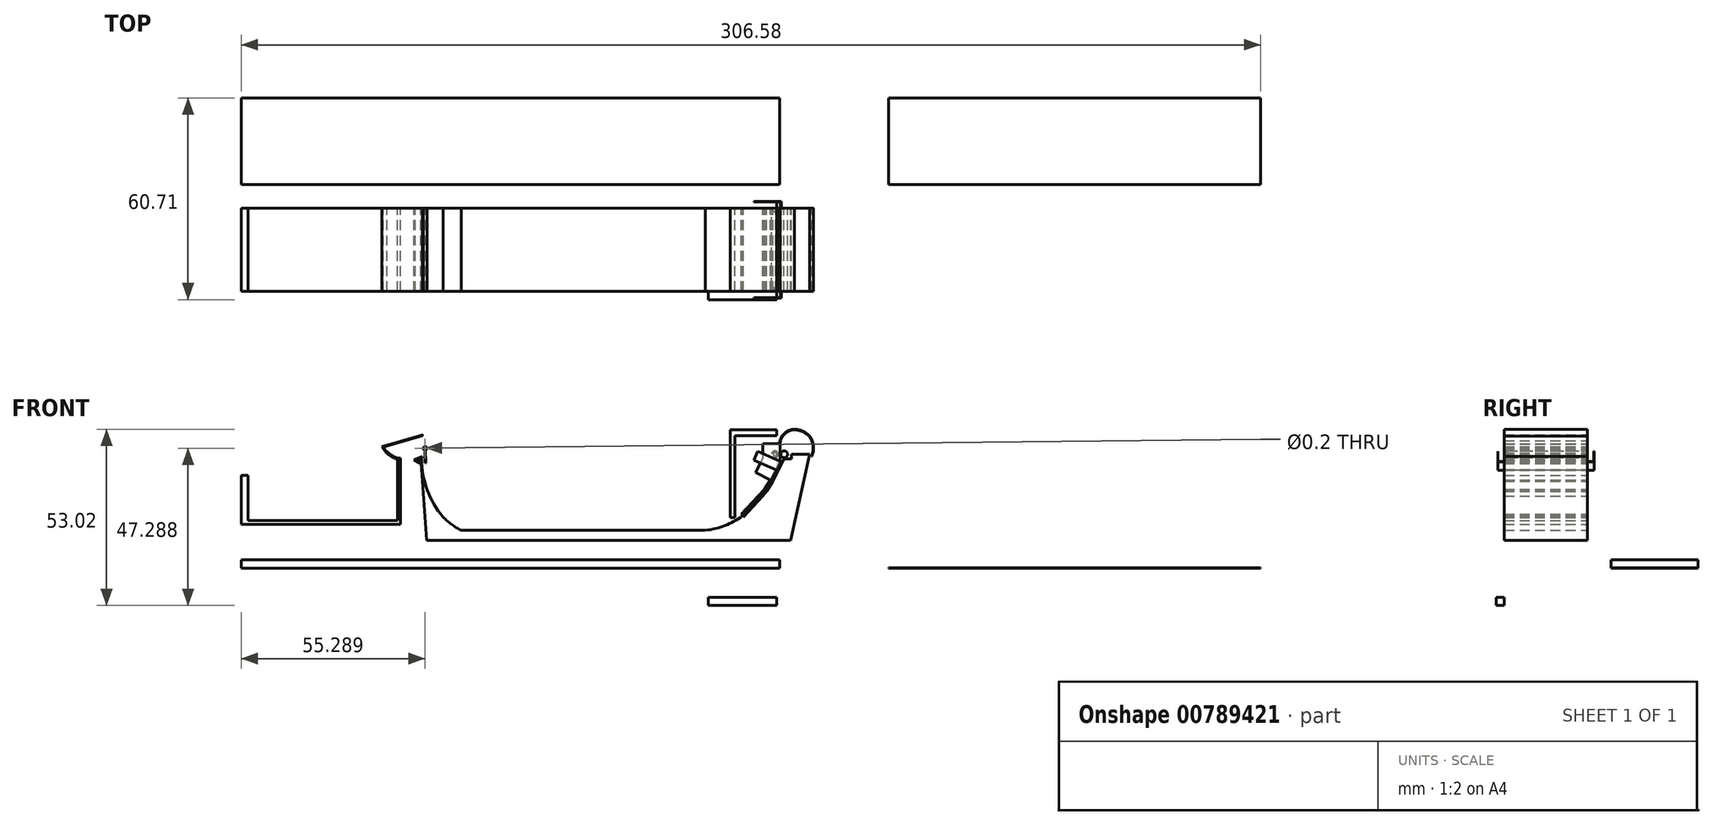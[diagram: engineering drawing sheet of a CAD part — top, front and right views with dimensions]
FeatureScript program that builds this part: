
annotation { "Feature Type Name" : "Feature", "Feature Type Description" : "" }
export const myFeature = defineFeature(function(context is Context, id is Id, definition is map)
    precondition{}
    {
        {
            var Q0;
            Q0=qCreatedBy(makeId("Front.planeOp"),FACE);
            var sketch = newSketch(context, id + "F0", { "sketchPlane" : qUnion([Q0])});
            skLineSegment(sketch, "E0", {"start": v(-36.24, 27.85) * mm, "end": v(-38.27, 27.85) * mm});
            skLineSegment(sketch, "E1", {"start": v(-38.27, 27.85) * mm, "end": v(-38.27, 17.8) * mm});
            skPoint(sketch, "E2.startSnap0", {"position": v(14.17, 40.62) * mm});
            skPoint(sketch, "E3.second.point", {"position": v(15.63, 39.33) * mm});
            skPoint(sketch, "E3.third.point", {"position": v(16.42, 39.16) * mm});
            skPoint(sketch, "E4.end.orphan", {"position": v(0, 14.33) * mm});
            skLineSegment(sketch, "E5", {"start": v(-36.24, 27.85) * mm, "end": v(-36.24, 19.36) * mm});
            skPoint(sketch, "E6.orphan", {"position": v(-34.21, 27.85) * mm});
            skPoint(sketch, "E7.centerSnap0", {"position": v(17.02, 36.74) * mm});
            skPoint(sketch, "E8.orphan", {"position": v(17.66, 36.74) * mm});
            skPoint(sketch, "E9.orphan", {"position": v(16.38, 36.74) * mm});
            skPoint(sketch, "E10.orphan", {"position": v(17.66, 36.62) * mm});
            skPoint(sketch, "E11.start.orphan", {"position": v(16.38, 36.62) * mm});
            skLineSegment(sketch, "E12", {"start": v(15.74, 32.9) * mm, "end": v(15.83, 31.65) * mm});
            skLineSegment(sketch, "E13", {"start": v(17.46, 8.3) * mm, "end": v(83.3, 8.3) * mm});
            skLineSegment(sketch, "E14", {"start": v(83.3, 8.3) * mm, "end": v(127.03, 8.3) * mm});
            skLineSegment(sketch, "E15", {"start": v(127.03, 8.3) * mm, "end": v(132.63, 34.27) * mm});
            skLineSegment(sketch, "E16", {"start": v(101.32, 11.34) * mm, "end": v(27.93, 11.34) * mm});
            skArc(sketch, "E17", {"start": v(15.97, 32.9) * mm, "mid": v(17.65, 23.56) * mm, "end": v(22.41, 15.34) * mm});
            skLineSegment(sketch, "E18", {"start": v(15.97, 32.9) * mm, "end": v(15.74, 32.9) * mm});
            skPoint(sketch, "E19.orphan", {"position": v(17.66, 36.03) * mm});
            skPoint(sketch, "E20.orphan", {"position": v(16.38, 36.03) * mm});
            skPoint(sketch, "E21.start.orphan", {"position": v(15.63, 40.62) * mm});
            skLineSegment(sketch, "E22", {"start": v(16.94, 35.48) * mm, "end": v(16.96, 35.48) * mm});
            skPoint(sketch, "E23.start.orphan", {"position": v(16.96, 31.74) * mm});
            skArc(sketch, "E24", {"start": v(16.18, 39.88) * mm, "mid": v(16.3, 39.98) * mm, "end": v(16.18, 40.08) * mm});
            skCircle(sketch, "E25", {"center": v(17.02, 36.03) * mm, "radius": 0.1 * mm});
            skLineSegment(sketch, "E26", {"start": v(17.16, 31.54) * mm, "end": v(17.09, 31.54) * mm});
            skLineSegment(sketch, "E27", {"start": v(17.09, 31.54) * mm, "end": v(17.04, 35.85) * mm});
            skLineSegment(sketch, "E28", {"start": v(17.04, 35.85) * mm, "end": v(17, 35.84) * mm});
            skLineSegment(sketch, "E29", {"start": v(17, 35.84) * mm, "end": v(17.04, 31.54) * mm});
            skLineSegment(sketch, "E30", {"start": v(17.04, 31.54) * mm, "end": v(16.96, 31.54) * mm});
            skLineSegment(sketch, "E31", {"start": v(16.96, 31.54) * mm, "end": v(16.94, 35.49) * mm});
            skLineSegment(sketch, "E32", {"start": v(13.75, 43.8) * mm, "end": v(16.18, 40.08) * mm});
            skPoint(sketch, "E33.start.orphan", {"position": v(1.3, 38.23) * mm});
            skPoint(sketch, "E34.end.orphan", {"position": v(2.06, 38.23) * mm});
            skPoint(sketch, "E35.orphan", {"position": v(15.34, 39.98) * mm});
            skPoint(sketch, "E36.start.orphan", {"position": v(17.02, 36.62) * mm});
            skPoint(sketch, "E37.trimOffspring.end.orphan", {"position": v(17.58, 36.03) * mm});
            skArc(sketch, "E38", {"start": v(17.14, 35.5) * mm, "mid": v(17, 36.57) * mm, "end": v(16.94, 35.49) * mm});
            skLineSegment(sketch, "E39", {"start": v(17.14, 35.5) * mm, "end": v(17.21, 31.54) * mm});
            skLineSegment(sketch, "E40", {"start": v(17.21, 31.54) * mm, "end": v(17.16, 31.54) * mm});
            skPoint(sketch, "E41.orphan", {"position": v(2.06, 39.98) * mm});
            skArc(sketch, "E42", {"start": v(22.41, 15.34) * mm, "mid": v(25, 13.1) * mm, "end": v(27.93, 11.34) * mm});
            skLineSegment(sketch, "E43", {"start": v(106.36, 11.34) * mm, "end": v(106.36, 11.34) * mm});
            skPoint(sketch, "E44.end.orphan", {"position": v(2.65, 14.33) * mm});
            skPoint(sketch, "E44.start.orphan", {"position": v(2.65, 11.02) * mm});
            skPoint(sketch, "E45.end.orphan", {"position": v(0, 8.98) * mm});
            skPoint(sketch, "E45.start.orphan", {"position": v(4.08, 8.98) * mm});
            skPoint(sketch, "E46.end.orphan", {"position": v(-16.48, 8.98) * mm});
            skPoint(sketch, "E47.start.orphan", {"position": v(-36.24, 10.87) * mm});
            skPoint(sketch, "E48.end.orphan", {"position": v(-38.27, 8.98) * mm});
            skPoint(sketch, "E48.start.orphan", {"position": v(-38.27, 14.33) * mm});
            skLineSegment(sketch, "E49", {"start": v(4.08, 13.15) * mm, "end": v(-38.27, 13.15) * mm});
            skLineSegment(sketch, "E50", {"start": v(-38.27, 13.15) * mm, "end": v(-38.27, 17.8) * mm});
            skLineSegment(sketch, "E51", {"start": v(-36.24, 17.8) * mm, "end": v(-36.24, 14.33) * mm});
            skLineSegment(sketch, "E52", {"start": v(-36.24, 13.15) * mm, "end": v(2.65, 13.15) * mm});
            skLineSegment(sketch, "E53", {"start": v(-36.24, 14.33) * mm, "end": v(2.65, 14.33) * mm});
            skLineSegment(sketch, "E54", {"start": v(-36.24, 17.8) * mm, "end": v(-36.24, 19.36) * mm});
            skPoint(sketch, "E55.orphan", {"position": v(11.11, 39.83) * mm});
            skPoint(sketch, "E56.orphan", {"position": v(2.68, 38.35) * mm});
            skPoint(sketch, "E57.orphan", {"position": v(2.86, 38.35) * mm});
            skLineSegment(sketch, "E58", {"start": v(3.18, 14.33) * mm, "end": v(2.65, 14.33) * mm});
            skLineSegment(sketch, "E59", {"start": v(4.08, 13.15) * mm, "end": v(5.21, 13.15) * mm});
            skLineSegment(sketch, "E60", {"start": v(3.18, 14.33) * mm, "end": v(4.08, 14.33) * mm});
            skPoint(sketch, "E61.start.orphan", {"position": v(4.08, 34.96) * mm});
            skPoint(sketch, "E62.orphan", {"position": v(4.08, 34.48) * mm});
            skLineSegment(sketch, "E63", {"start": v(16.18, 39.88) * mm, "end": v(6.67, 37.05) * mm});
            skLineSegment(sketch, "E64", {"start": v(16.18, 40.08) * mm, "end": v(15.51, 39.87) * mm});
            skLineSegment(sketch, "E65", {"start": v(15.51, 39.87) * mm, "end": v(6.6, 37.22) * mm});
            skLineSegment(sketch, "E66", {"start": v(6.6, 37.22) * mm, "end": v(4.09, 36.47) * mm});
            skPoint(sketch, "E66.endSnap0", {"position": v(3.22, 38.25) * mm});
            skLineSegment(sketch, "E67", {"start": v(6.67, 37.05) * mm, "end": v(4.41, 36.38) * mm});
            skArc(sketch, "E68", {"start": v(5.56, 34.55) * mm, "mid": v(5.56, 34.55) * mm, "end": v(5.57, 34.55) * mm});
            skLineSegment(sketch, "E69", {"start": v(5.57, 34.55) * mm, "end": v(5.57, 34.54) * mm});
            skPoint(sketch, "E70.orphan", {"position": v(13.65, 39.85) * mm});
            skPoint(sketch, "E71.start.orphan", {"position": v(3.22, 36.22) * mm});
            skLineSegment(sketch, "E72", {"start": v(4.08, 14.33) * mm, "end": v(8.74, 14.33) * mm});
            skLineSegment(sketch, "E73", {"start": v(8.74, 14.33) * mm, "end": v(8.74, 32.67) * mm});
            skLineSegment(sketch, "E74", {"start": v(8.74, 33.1) * mm, "end": v(9.64, 33.1) * mm});
            skLineSegment(sketch, "E75", {"start": v(9.64, 33.1) * mm, "end": v(9.64, 13.15) * mm});
            skLineSegment(sketch, "E76", {"start": v(9.64, 13.15) * mm, "end": v(5.21, 13.15) * mm});
            skArc(sketch, "E77", {"start": v(4.41, 36.38) * mm, "mid": v(6.3, 34.38) * mm, "end": v(8.74, 33.1) * mm});
            skArc(sketch, "E78", {"start": v(4.09, 36.47) * mm, "mid": v(6.04, 34.12) * mm, "end": v(8.74, 32.67) * mm});
            skArc(sketch, "E79", {"start": v(101.32, 11.34) * mm, "mid": v(107.16, 12.76) * mm, "end": v(112.43, 15.65) * mm});
            skCircle(sketch, "E80", {"center": v(122.26, 34.23) * mm, "radius": 1 * mm});
            skLineSegment(sketch, "E81", {"start": v(110.26, 39.86) * mm, "end": v(110.26, 15.22) * mm});
            skLineSegment(sketch, "E82", {"start": v(110.26, 15.22) * mm, "end": v(108.83, 15.22) * mm});
            skLineSegment(sketch, "E83", {"start": v(108.83, 15.22) * mm, "end": v(108.83, 39.86) * mm});
            skLineSegment(sketch, "E84", {"start": v(108.83, 39.86) * mm, "end": v(108.83, 41.61) * mm});
            skLineSegment(sketch, "E85", {"start": v(108.83, 41.61) * mm, "end": v(122.82, 41.61) * mm});
            skCircle(sketch, "E86", {"center": v(125.03, 34.23) * mm, "radius": 1.03 * mm});
            skLineSegment(sketch, "E87", {"start": v(127.23, 34.27) * mm, "end": v(127.23, 32.8) * mm});
            skLineSegment(sketch, "E88", {"start": v(127.23, 32.8) * mm, "end": v(124.93, 32.8) * mm});
            skLineSegment(sketch, "E89", {"start": v(123.58, 37.49) * mm, "end": v(123.58, 32.21) * mm});
            skLineSegment(sketch, "E90", {"start": v(123.74, 32.21) * mm, "end": v(123.74, 37.22) * mm});
            skLineSegment(sketch, "E91", {"start": v(122.82, 41.61) * mm, "end": v(122.82, 39.86) * mm});
            skLineSegment(sketch, "E92.trimOffspring", {"start": v(122.82, 39.86) * mm, "end": v(110.26, 39.86) * mm});
            skArc(sketch, "E93", {"start": v(128.06, 41.59) * mm, "mid": v(125.07, 40.23) * mm, "end": v(123.74, 37.22) * mm});
            skArc(sketch, "E94", {"start": v(132.54, 39.67) * mm, "mid": v(130.48, 41.05) * mm, "end": v(128.06, 41.59) * mm});
            skArc(sketch, "E95", {"start": v(133.2, 33.63) * mm, "mid": v(133.7, 36.74) * mm, "end": v(132.54, 39.67) * mm});
            skArc(sketch, "E96", {"start": v(133.37, 33.63) * mm, "mid": v(133.79, 36.77) * mm, "end": v(132.69, 39.74) * mm});
            skArc(sketch, "E97", {"start": v(132.69, 39.74) * mm, "mid": v(130.57, 41.2) * mm, "end": v(128.06, 41.76) * mm});
            skArc(sketch, "E98", {"start": v(128.06, 41.76) * mm, "mid": v(125.33, 40.75) * mm, "end": v(123.74, 38.31) * mm});
            skLineSegment(sketch, "E99", {"start": v(133.2, 33.63) * mm, "end": v(133.37, 33.63) * mm});
            skFitSpline(sketch, "E100", {"points": [v(123.74, 38.31) * mm, v(123.58, 37.45) * mm, v(123.58, 37.49) * mm, v(123.58, 37.86) * mm], "startDerivative": vector(-0.4, -2.37) * mm, "endDerivative": vector(0, 1.27) * mm});
            skPoint(sketch, "E101.end.orphan", {"position": v(123.58, 39.58) * mm});
            skPoint(sketch, "E101.start.orphan", {"position": v(123.74, 39.58) * mm});
            skLineSegment(sketch, "E102", {"start": v(127.23, 34.27) * mm, "end": v(132.63, 34.27) * mm});
            skPoint(sketch, "E103.end.orphan", {"position": v(127.23, 36.3) * mm});
            skLineSegment(sketch, "E104", {"start": v(123.58, 32.21) * mm, "end": v(122.49, 29.63) * mm});
            skLineSegment(sketch, "E105", {"start": v(123.74, 32.21) * mm, "end": v(122.62, 29.57) * mm});
            skLineSegment(sketch, "E106", {"start": v(122.62, 29.57) * mm, "end": v(121.09, 26.45) * mm});
            skLineSegment(sketch, "E107", {"start": v(120.93, 26.52) * mm, "end": v(122.49, 29.63) * mm});
            skLineSegment(sketch, "E108", {"start": v(121.09, 26.45) * mm, "end": v(119.27, 23.56) * mm});
            skLineSegment(sketch, "E109", {"start": v(119.07, 23.69) * mm, "end": v(120.93, 26.52) * mm});
            skLineSegment(sketch, "E110", {"start": v(119.27, 23.56) * mm, "end": v(112.33, 15.9) * mm});
            skLineSegment(sketch, "E111", {"start": v(112.33, 15.9) * mm, "end": v(112.07, 16.14) * mm});
            skLineSegment(sketch, "E112", {"start": v(112.07, 16.14) * mm, "end": v(119.07, 23.69) * mm});
            skLineSegment(sketch, "E113", {"start": v(112.58, 15.51) * mm, "end": v(112.43, 15.65) * mm});
            skLineSegment(sketch, "E114", {"start": v(124.93, 32.8) * mm, "end": v(121.63, 26.17) * mm});
            skLineSegment(sketch, "E115", {"start": v(121.63, 26.17) * mm, "end": v(119.75, 23.08) * mm});
            skLineSegment(sketch, "E116", {"start": v(119.75, 23.08) * mm, "end": v(118.52, 21.7) * mm});
            skLineSegment(sketch, "E117", {"start": v(118.52, 21.7) * mm, "end": v(114.05, 16.77) * mm});
            skLineSegment(sketch, "E118", {"start": v(114.05, 16.77) * mm, "end": v(112.74, 15.32) * mm});
            skLineSegment(sketch, "E119", {"start": v(112.74, 15.32) * mm, "end": v(112.58, 15.51) * mm});
            skLineSegment(sketch, "E120", {"start": v(123.94, 32.07) * mm, "end": v(122.8, 29.48) * mm});
            skLineSegment(sketch, "E121", {"start": v(122.8, 29.48) * mm, "end": v(122.96, 29.4) * mm});
            skLineSegment(sketch, "E122", {"start": v(122.96, 29.4) * mm, "end": v(124.2, 31.92) * mm});
            skLineSegment(sketch, "E123", {"start": v(124.2, 31.92) * mm, "end": v(123.94, 32.07) * mm});
            skArc(sketch, "E124", {"start": v(14.12, 32.5) * mm, "mid": v(14.94, 32) * mm, "end": v(15.83, 31.65) * mm});
            skArc(sketch, "E125", {"start": v(13.68, 32.53) * mm, "mid": v(14.7, 31.87) * mm, "end": v(15.84, 31.4) * mm});
            skLineSegment(sketch, "E126.trimOffspring", {"start": v(15.84, 31.4) * mm, "end": v(17.46, 8.3) * mm});
            skLineSegment(sketch, "E127", {"start": v(14.12, 32.5) * mm, "end": v(16.04, 33.27) * mm});
            skPoint(sketch, "E127.startSnap0", {"position": v(14.28, 32.4) * mm});
            skArc(sketch, "E128", {"start": v(16.03, 33.27) * mm, "mid": v(16.09, 33.4) * mm, "end": v(15.95, 33.45) * mm});
            skPoint(sketch, "E129.orphan", {"position": v(13.86, 32.4) * mm});
            skLineSegment(sketch, "E130", {"start": v(15.97, 33.46) * mm, "end": v(13.68, 32.53) * mm});
            skSolve(sketch);
        }
        {
            var Q0;
            Q0=makeQuery(id+"F0.imprint","IMPRINT",FACE,{"disambiguationData":[TD([[makeQuery(id+"F0.imprint","IMPRINT",EDGE,{"derivedFrom":sQuery(id+"F0.wireOp",EDGE,"E24")}),1.0]])]});
            extrude(context, id + "F1", {"entities" : qUnion([Q0]), "depth" : 25 * mm, "offsetDistance" : 25 * mm});
        }
        {
            var Q0;
            Q0=makeQuery(id+"F0.imprint","IMPRINT",FACE,{"disambiguationData":[TD([[makeQuery(id+"F0.imprint","IMPRINT",EDGE,{"derivedFrom":sQuery(id+"F0.wireOp",EDGE,"E25")}),-1.0]])]});
            extrude(context, id + "F2", {"entities" : qUnion([Q0]), "depth" : 25 * mm, "offsetDistance" : 25 * mm});
        }
        {
            var Q0;
            Q0=makeQuery(id+"F0.imprint","IMPRINT",FACE,{"disambiguationData":[TD([[makeQuery(id+"F0.imprint","IMPRINT",EDGE,{"derivedFrom":sQuery(id+"F0.wireOp",EDGE,"E12")}),1.0]])]});
            extrude(context, id + "F3", {"entities" : qUnion([Q0]), "depth" : 25 * mm, "offsetDistance" : 25 * mm});
        }
        {
            var Q0;
            Q0=qCreatedBy(makeId("Top.planeOp"),FACE);
            var sketch = newSketch(context, id + "F4", { "sketchPlane" : qUnion([Q0])});
            skLineSegment(sketch, "E131.bottom", {"start": v(-38.21, 33.2) * mm, "end": v(79.97, 33.2) * mm});
            skLineSegment(sketch, "E131.top", {"start": v(-38.21, 7.08) * mm, "end": v(79.97, 7.08) * mm});
            skLineSegment(sketch, "E131.left", {"start": v(-38.21, 33.2) * mm, "end": v(-38.21, 7.08) * mm});
            skLineSegment(sketch, "E132", {"start": v(62.88, 33.2) * mm, "end": v(123.68, 33.2) * mm});
            skLineSegment(sketch, "E133", {"start": v(123.68, 33.2) * mm, "end": v(123.68, 7.08) * mm});
            skLineSegment(sketch, "E134", {"start": v(123.68, 7.08) * mm, "end": v(79.97, 7.08) * mm});
            skLineSegment(sketch, "E135.bottom", {"start": v(156.42, 33.2) * mm, "end": v(268.31, 33.2) * mm});
            skLineSegment(sketch, "E135.top", {"start": v(156.42, 7.08) * mm, "end": v(268.31, 7.08) * mm});
            skLineSegment(sketch, "E135.left", {"start": v(156.42, 33.2) * mm, "end": v(156.42, 7.08) * mm});
            skLineSegment(sketch, "E135.right", {"start": v(268.31, 33.2) * mm, "end": v(268.31, 7.08) * mm});
            skSolve(sketch);
        }
        {
            var Q0;
            Q0=makeQuery(id+"F4.imprint","IMPRINT",FACE,{"disambiguationData":[TD([[makeQuery(id+"F4.imprint","IMPRINT",EDGE,{"derivedFrom":sQuery(id+"F4.wireOp",EDGE,"E131.bottom")}),-1.0]])]});
            extrude(context, id + "F5", {"entities" : qUnion([Q0]), "depth" : 2.5 * mm, "offsetDistance" : 25 * mm});
        }
        {
            var Q0;
            Q0=makeQuery(id+"F5.opExtrude","CAP_FACE",FACE,{"disambiguationData":[OSD([sQuery(id+"F4.wireOp",EDGE,"E131.bottom"),sQuery(id+"F4.wireOp",EDGE,"E131.top"),sQuery(id+"F4.wireOp",EDGE,"E131.left"),sQuery(id+"F4.wireOp",EDGE,"E132"),sQuery(id+"F4.wireOp",EDGE,"E133"),sQuery(id+"F4.wireOp",EDGE,"E134")])],"isStart":false});
            var sketch = newSketch(context, id + "F6", { "sketchPlane" : qUnion([Q0])});
            skLineSegment(sketch, "E136.bottom", {"start": v(-38.21, 33.2) * mm, "end": v(2.43, 33.2) * mm});
            skLineSegment(sketch, "E136.top", {"start": v(-38.21, 7.08) * mm, "end": v(2.43, 7.08) * mm});
            skLineSegment(sketch, "E136.left", {"start": v(-38.21, 33.2) * mm, "end": v(-38.21, 7.08) * mm});
            skLineSegment(sketch, "E136.right", {"start": v(2.43, 33.2) * mm, "end": v(2.43, 7.08) * mm});
            skSolve(sketch);
        }
        {
            var Q0;
            Q0=makeQuery(id+"F4.imprint","IMPRINT",FACE,{"disambiguationData":[TD([[makeQuery(id+"F4.imprint","IMPRINT",EDGE,{"derivedFrom":sQuery(id+"F4.wireOp",EDGE,"E135.bottom")}),-1.0]])]});
            extrude(context, id + "F7", {"entities" : qUnion([Q0]), "depth" : 0.1 * mm, "offsetDistance" : 25 * mm});
        }
        {
            var Q0;
            Q0=makeQuery(id+"F7.opExtrude","CAP_FACE",FACE,{"disambiguationData":[OSD([sQuery(id+"F4.wireOp",EDGE,"E135.bottom"),sQuery(id+"F4.wireOp",EDGE,"E135.top"),sQuery(id+"F4.wireOp",EDGE,"E135.left"),sQuery(id+"F4.wireOp",EDGE,"E135.right")])],"isStart":false});
            var sketch = newSketch(context, id + "F8", { "sketchPlane" : qUnion([Q0])});
            skLineSegment(sketch, "E137", {"start": v(161.42, 33.2) * mm, "end": v(161.42, 7.08) * mm});
            skSolve(sketch);
        }
        {
            var Q0;
            Q0=makeQuery(id+"F0.imprint","IMPRINT",FACE,{"disambiguationData":[TD([[makeQuery(id+"F0.imprint","IMPRINT",EDGE,{"derivedFrom":sQuery(id+"F0.wireOp",EDGE,"E80")}),1.0]])]});
            extrude(context, id + "F9", {"entities" : qUnion([Q0]), "depth" : 24 * mm, "offsetDistance" : 25 * mm});
        }
        {
            var Q0;
            Q0=makeQuery(id+"F0.imprint","IMPRINT",FACE,{"disambiguationData":[TD([[makeQuery(id+"F0.imprint","IMPRINT",EDGE,{"derivedFrom":sQuery(id+"F0.wireOp",EDGE,"E86")}),1.0]])]});
            extrude(context, id + "F10", {"entities" : qUnion([Q0]), "depth" : 25 * mm, "offsetDistance" : 25 * mm});
        }
        {
            var Q0;
            Q0=makeQuery(id+"F0.imprint","IMPRINT",FACE,{"disambiguationData":[TD([[makeQuery(id+"F0.imprint","IMPRINT",EDGE,{"derivedFrom":sQuery(id+"F0.wireOp",EDGE,"E89")}),1.0]])]});
            extrude(context, id + "F11", {"entities" : qUnion([Q0]), "depth" : 25 * mm, "offsetDistance" : 25 * mm});
        }
        {
            var Q0;
            Q0=makeQuery(id+"F3.opExtrude","CAP_FACE",FACE,{"disambiguationData":[OSD([sQuery(id+"F0.wireOp",EDGE,"E12"),sQuery(id+"F0.wireOp",EDGE,"E13"),sQuery(id+"F0.wireOp",EDGE,"E14"),sQuery(id+"F0.wireOp",EDGE,"E15"),sQuery(id+"F0.wireOp",EDGE,"w4MDjuLF-quGd-ABje-a59T-MTtNCKjQTqCC"),sQuery(id+"F0.wireOp",EDGE,"1qvucnDc-VQm0-8KhS-z7SF-FsArdJ4ZOjVe"),sQuery(id+"F0.wireOp",EDGE,"E16"),sQuery(id+"F0.wireOp",EDGE,"E17"),sQuery(id+"F0.wireOp",EDGE,"E18"),sQuery(id+"F0.wireOp",EDGE,"E42"),sQuery(id+"F0.wireOp",EDGE,"E79"),sQuery(id+"F0.wireOp",EDGE,"gqOQFJSQ-Navi-1Wbq-EMwf-l3DRoNK6dP6c"),sQuery(id+"F0.wireOp",EDGE,"E81"),sQuery(id+"F0.wireOp",EDGE,"E82"),sQuery(id+"F0.wireOp",EDGE,"E83"),sQuery(id+"F0.wireOp",EDGE,"E84"),sQuery(id+"F0.wireOp",EDGE,"E85"),sQuery(id+"F0.wireOp",EDGE,"473c3927-8e2a-4cfb-948c-3dfecc8dc65e.trimOffspring"),sQuery(id+"F0.wireOp",EDGE,"E103"),sQuery(id+"F0.wireOp",EDGE,"E87"),sQuery(id+"F0.wireOp",EDGE,"E88"),sQuery(id+"F0.wireOp",EDGE,"4562d8f3-b021-441a-b61c-79b72f4f745d.trimOffspring")])],"isStart":false});
            var sketch = newSketch(context, id + "F12", { "sketchPlane" : qUnion([Q0])});
            skLineSegment(sketch, "E138", {"start": v(127.03, 8.3) * mm, "end": v(122.8, -11.26) * mm});
            skLineSegment(sketch, "E139", {"start": v(122.8, -11.26) * mm, "end": v(120.3, -11.26) * mm});
            skLineSegment(sketch, "E140", {"start": v(122.8, -11.26) * mm, "end": v(122.8, -8.76) * mm});
            skLineSegment(sketch, "E141", {"start": v(122.8, -8.76) * mm, "end": v(120.3, -8.76) * mm});
            skLineSegment(sketch, "E142", {"start": v(120.3, -8.76) * mm, "end": v(120.3, -11.26) * mm});
            skLineSegment(sketch, "E143", {"start": v(120.3, -11.26) * mm, "end": v(122.8, -11.26) * mm});
            skSolve(sketch);
        }
        {
            var Q0;
            Q0=makeQuery(id+"F12.imprint","IMPRINT",FACE,{"disambiguationData":[TD([[makeQuery(id+"F12.imprint","IMPRINT",EDGE,{"derivedFrom":sQuery(id+"F12.wireOp",EDGE,"E140")}),1.0]])]});
            extrude(context, id + "F13", {"entities" : qUnion([Q0]), "operationType" : NewBodyOperationType.ADD, "depth" : 2.5 * mm, "offsetDistance" : 25 * mm});
        }
        {
            var Q0;
            Q0=makeQuery(id+"F13.opExtrude","SWEPT_FACE",FACE,{"disambiguationData":[OSD([sQuery(id+"F12.wireOp",EDGE,"E142")])]});
            extrude(context, id + "F14", {"entities" : qUnion([Q0]), "operationType" : NewBodyOperationType.ADD, "depth" : 18.1 * mm, "offsetDistance" : 25 * mm});
        }
        {
            var Q0;
            Q0=makeQuery(id+"F0.imprint","IMPRINT",FACE,{"disambiguationData":[TD([[makeQuery(id+"F0.imprint","IMPRINT",EDGE,{"derivedFrom":sQuery(id+"F0.wireOp",EDGE,"E81")}),-1.0]])]});
            extrude(context, id + "F15", {"entities" : qUnion([Q0]), "operationType" : NewBodyOperationType.ADD, "depth" : 25 * mm, "offsetDistance" : 25 * mm});
        }
        {
            var Q0;
            Q0=makeQuery(id+"F0.imprint","IMPRINT",FACE,{"disambiguationData":[TD([[makeQuery(id+"F0.imprint","IMPRINT",EDGE,{"derivedFrom":sQuery(id+"F0.wireOp",EDGE,"E80")}),1.0]])]});
            extrude(context, id + "F16", {"entities" : qUnion([Q0]), "operationType" : NewBodyOperationType.REMOVE, "depth" : 1 * mm, "offsetDistance" : 25 * mm});
        }
        {
            var Q0;
            Q0=makeQuery(id+"F11.opExtrude","SWEPT_FACE",FACE,{"disambiguationData":[OSD([sQuery(id+"F0.wireOp",EDGE,"E89")])]});
            var sketch = newSketch(context, id + "F17", { "sketchPlane" : qUnion([Q0])});
            skLineSegment(sketch, "E144", {"start": v(24.9, 32.21) * mm, "end": v(24.9, 37.45) * mm});
            skLineSegment(sketch, "E145", {"start": v(24.9, 37.45) * mm, "end": v(25, 37.45) * mm});
            skLineSegment(sketch, "E146", {"start": v(25, 37.45) * mm, "end": v(25, 32.21) * mm});
            skLineSegment(sketch, "E147", {"start": v(25, 32.21) * mm, "end": v(24.9, 32.21) * mm});
            skLineSegment(sketch, "E148", {"start": v(0, 32.21) * mm, "end": v(0, 37.45) * mm});
            skLineSegment(sketch, "E149", {"start": v(0, 37.45) * mm, "end": v(0.1, 37.45) * mm});
            skLineSegment(sketch, "E150", {"start": v(0.1, 37.45) * mm, "end": v(0.1, 32.21) * mm});
            skLineSegment(sketch, "E151", {"start": v(0.1, 32.21) * mm, "end": v(0, 32.21) * mm});
            skSolve(sketch);
        }
        {
            var Q0;
            Q0=makeQuery(id+"F17.imprint","IMPRINT",FACE,{"disambiguationData":[TD([[makeQuery(id+"F17.imprint","IMPRINT",EDGE,{"derivedFrom":sQuery(id+"F17.wireOp",EDGE,"E144")}),-1.0]])]});
            extrude(context, id + "F18", {"entities" : qUnion([Q0]), "operationType" : NewBodyOperationType.ADD, "depth" : 5 * mm, "offsetDistance" : 25 * mm});
        }
        {
            var Q0;
            Q0=makeQuery(id+"F17.imprint","IMPRINT",FACE,{"disambiguationData":[TD([[makeQuery(id+"F17.imprint","IMPRINT",EDGE,{"derivedFrom":sQuery(id+"F17.wireOp",EDGE,"E148")}),1.0]])]});
            extrude(context, id + "F19", {"entities" : qUnion([Q0]), "operationType" : NewBodyOperationType.ADD, "depth" : 5 * mm, "offsetDistance" : 25 * mm});
        }
        {
            var Q0;
            Q0=makeQuery(id+"F11.opExtrude","SWEPT_FACE",FACE,{"disambiguationData":[OSD([sQuery(id+"F0.wireOp",EDGE,"E104")])]});
            var sketch = newSketch(context, id + "F20", { "sketchPlane" : qUnion([Q0])});
            skLineSegment(sketch, "E152", {"start": v(24.9, 77.88) * mm, "end": v(24.9, 75.07) * mm});
            skLineSegment(sketch, "E153", {"start": v(24.9, 75.07) * mm, "end": v(25, 75.07) * mm});
            skLineSegment(sketch, "E154", {"start": v(25, 75.07) * mm, "end": v(25, 77.88) * mm});
            skLineSegment(sketch, "E155", {"start": v(25, 77.88) * mm, "end": v(24.9, 77.88) * mm});
            skLineSegment(sketch, "E156", {"start": v(0.1, 77.88) * mm, "end": v(0.1, 75.07) * mm});
            skLineSegment(sketch, "E157", {"start": v(0.1, 75.07) * mm, "end": v(0, 75.07) * mm});
            skLineSegment(sketch, "E158", {"start": v(0, 75.07) * mm, "end": v(0, 77.88) * mm});
            skLineSegment(sketch, "E159", {"start": v(0, 77.88) * mm, "end": v(0.1, 77.88) * mm});
            skSolve(sketch);
        }
        {
            var Q0;
            Q0=makeQuery(id+"F20.imprint","IMPRINT",FACE,{"disambiguationData":[TD([[makeQuery(id+"F20.imprint","IMPRINT",EDGE,{"derivedFrom":sQuery(id+"F20.wireOp",EDGE,"E156")}),-1.0]])]});
            var Q1;
            Q1=makeQuery(id+"F20.imprint","IMPRINT",FACE,{"disambiguationData":[TD([[makeQuery(id+"F20.imprint","IMPRINT",EDGE,{"derivedFrom":sQuery(id+"F20.wireOp",EDGE,"E152")}),1.0]])]});
            extrude(context, id + "F21", {"entities" : qUnion([Q0, Q1]), "operationType" : NewBodyOperationType.ADD, "depth" : 5 * mm, "offsetDistance" : 25 * mm});
        }
        {
            var Q0;
            Q0=makeQuery(id+"F11.opExtrude","SWEPT_FACE",FACE,{"disambiguationData":[OSD([sQuery(id+"F0.wireOp",EDGE,"E107")])]});
            var sketch = newSketch(context, id + "F22", { "sketchPlane" : qUnion([Q0])});
            skLineSegment(sketch, "E160", {"start": v(0.1, 81.52) * mm, "end": v(0.1, 78.04) * mm});
            skLineSegment(sketch, "E161", {"start": v(0.1, 78.04) * mm, "end": v(0, 78.04) * mm});
            skLineSegment(sketch, "E162", {"start": v(0, 78.04) * mm, "end": v(0, 81.52) * mm});
            skLineSegment(sketch, "E163", {"start": v(0, 81.52) * mm, "end": v(0.1, 81.52) * mm});
            skLineSegment(sketch, "E164", {"start": v(24.9, 81.52) * mm, "end": v(24.9, 78.04) * mm});
            skLineSegment(sketch, "E165", {"start": v(24.9, 78.04) * mm, "end": v(25, 78.04) * mm});
            skLineSegment(sketch, "E166", {"start": v(25, 78.04) * mm, "end": v(25, 81.52) * mm});
            skLineSegment(sketch, "E167", {"start": v(25, 81.52) * mm, "end": v(24.9, 81.52) * mm});
            skSolve(sketch);
        }
        {
            var Q0;
            Q0=makeQuery(id+"F22.imprint","IMPRINT",FACE,{"disambiguationData":[TD([[makeQuery(id+"F22.imprint","IMPRINT",EDGE,{"derivedFrom":sQuery(id+"F22.wireOp",EDGE,"E164")}),1.0]])]});
            var Q1;
            Q1=makeQuery(id+"F22.imprint","IMPRINT",FACE,{"disambiguationData":[TD([[makeQuery(id+"F22.imprint","IMPRINT",EDGE,{"derivedFrom":sQuery(id+"F22.wireOp",EDGE,"E160")}),-1.0]])]});
            extrude(context, id + "F23", {"entities" : qUnion([Q0, Q1]), "operationType" : NewBodyOperationType.ADD, "depth" : 5 * mm, "offsetDistance" : 25 * mm});
        }
        {
            var Q0;
            Q0=makeQuery(id+"F9.opExtrude","CAP_FACE",FACE,{"disambiguationData":[OSD([sQuery(id+"F0.wireOp",EDGE,"E80")])],"isStart":false});
            var sketch = newSketch(context, id + "F24", { "sketchPlane" : qUnion([Q0])});
            skCircle(sketch, "E168", {"center": v(122.26, 34.23) * mm, "radius": 0.5 * mm});
            skSolve(sketch);
        }
        {
            var Q0;
            Q0=makeQuery(id+"F24.imprint","IMPRINT",FACE,{"disambiguationData":[TD([[makeQuery(id+"F24.imprint","IMPRINT",EDGE,{"derivedFrom":sQuery(id+"F24.wireOp",EDGE,"E168")}),1.0]])]});
            extrude(context, id + "F25", {"entities" : qUnion([Q0]), "operationType" : NewBodyOperationType.ADD, "depth" : 0.5 * mm, "offsetDistance" : 25 * mm});
        }
        {
            var Q0;
            Q0=makeQuery(id+"F0.imprint","IMPRINT",FACE,{"disambiguationData":[TD([[makeQuery(id+"F0.imprint","IMPRINT",EDGE,{"derivedFrom":sQuery(id+"F0.wireOp",EDGE,"E120")}),1.0]])]});
            extrude(context, id + "F26", {"entities" : qUnion([Q0]), "depth" : 27 * mm, "offsetDistance" : 25 * mm});
        }
        {
            var Q0;
            Q0=makeQuery(id+"F26.opExtrude","CAP_FACE",FACE,{"disambiguationData":[OSD([sQuery(id+"F0.wireOp",EDGE,"E120"),sQuery(id+"F0.wireOp",EDGE,"E121"),sQuery(id+"F0.wireOp",EDGE,"E122"),sQuery(id+"F0.wireOp",EDGE,"E123")])],"isStart":true});
            extrude(context, id + "F27", {"entities" : qUnion([Q0]), "operationType" : NewBodyOperationType.ADD, "depth" : 2 * mm, "offsetDistance" : 25 * mm});
        }
        {
            var Q0;
            {var subQ0=sQuery(id+"F0.wireOp",EDGE,"E120");Q0=makeQuery(id+"F27.boolean.opBoolean","MERGE",FACE,{"derivedFrom":[makeQuery(id+"F26.opExtrude","SWEPT_FACE",FACE,{"disambiguationData":[OSD([subQ0])]}),makeQuery(id+"F27.opExtrude","SWEPT_FACE",FACE,{"disambiguationData":[OSD([subQ0])]})]});}
            var sketch = newSketch(context, id + "F28", { "sketchPlane" : qUnion([Q0])});
            skLineSegment(sketch, "E169", {"start": v(-1.9, 79.5) * mm, "end": v(-1.9, 76.67) * mm});
            skLineSegment(sketch, "E170", {"start": v(-1.9, 76.67) * mm, "end": v(-2, 76.67) * mm});
            skLineSegment(sketch, "E171", {"start": v(-2, 76.67) * mm, "end": v(-2, 79.5) * mm});
            skLineSegment(sketch, "E172", {"start": v(-2, 79.5) * mm, "end": v(-1.9, 79.5) * mm});
            skLineSegment(sketch, "E173", {"start": v(26.9, 79.5) * mm, "end": v(26.9, 76.67) * mm});
            skLineSegment(sketch, "E174", {"start": v(26.9, 76.67) * mm, "end": v(27, 76.67) * mm});
            skLineSegment(sketch, "E175", {"start": v(27, 76.67) * mm, "end": v(27, 79.5) * mm});
            skLineSegment(sketch, "E176", {"start": v(27, 79.5) * mm, "end": v(26.9, 79.5) * mm});
            skSolve(sketch);
        }
        {
            var Q0;
            Q0=makeQuery(id+"F28.imprint","IMPRINT",FACE,{"disambiguationData":[TD([[makeQuery(id+"F28.imprint","IMPRINT",EDGE,{"derivedFrom":sQuery(id+"F28.wireOp",EDGE,"E173")}),1.0]])]});
            var Q1;
            Q1=makeQuery(id+"F28.imprint","IMPRINT",FACE,{"disambiguationData":[TD([[makeQuery(id+"F28.imprint","IMPRINT",EDGE,{"derivedFrom":sQuery(id+"F28.wireOp",EDGE,"E169")}),-1.0]])]});
            extrude(context, id + "F29", {"entities" : qUnion([Q0, Q1]), "operationType" : NewBodyOperationType.ADD, "depth" : 7.5 * mm, "offsetDistance" : 25 * mm});
        }
    });
